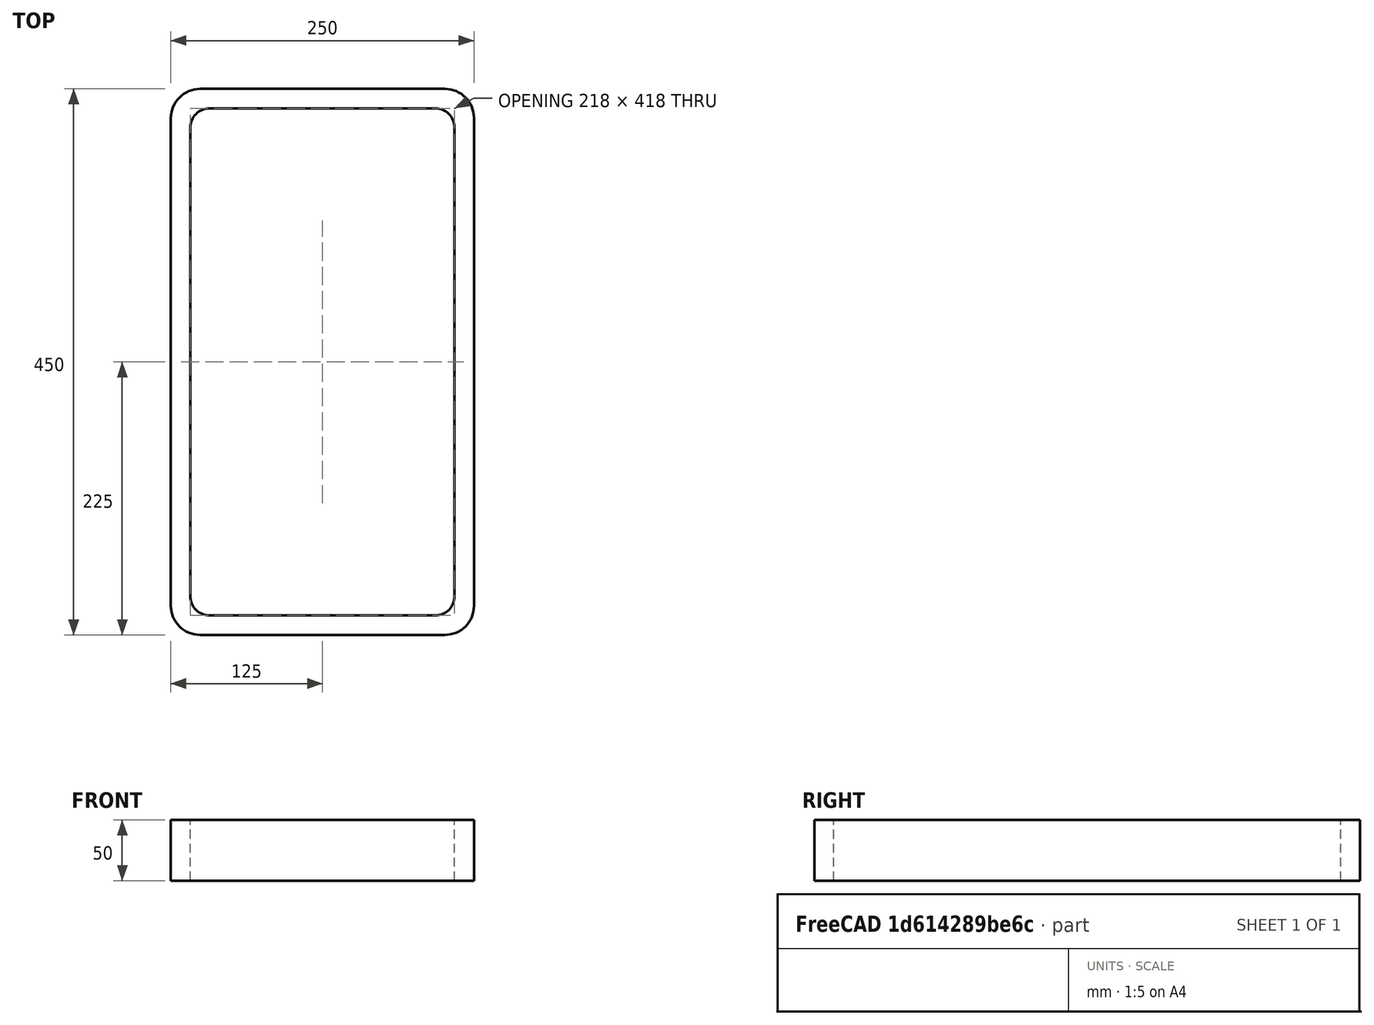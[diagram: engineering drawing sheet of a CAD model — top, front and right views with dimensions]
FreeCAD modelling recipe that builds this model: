
FCSTD DOCUMENT  (FreeCAD 0.15R4671 (Git))
Label: Rectangular hollow section 450x250x16 EN10219 S235JRH
License: All rights reserved
LicenseURL: http://en.wikipedia.org/wiki/All_rights_reserved
objects: Sketcher::SketchObject×1, Part::Extrusion×1
note: 2 computed .brp shape members not serialized (recipe doc carries the construction recipe); baked Part::Feature solids carry a one-line shape summary decoded from their .brp

FEATURE [Sketcher::SketchObject] Sketch
  sketch-geometry (16):
    g0: LineSegment StartX=-93 StartY=209 StartZ=0 EndX=93 EndY=209 EndZ=0
    g1: LineSegment StartX=109 StartY=193 StartZ=0 EndX=109 EndY=-193 EndZ=0
    g2: LineSegment StartX=93 StartY=-209 StartZ=0 EndX=-93 EndY=-209 EndZ=0
    g3: LineSegment StartX=-109 StartY=-193 StartZ=0 EndX=-109 EndY=193 EndZ=0
    g4: LineSegment StartX=-101 StartY=225 StartZ=0 EndX=101 EndY=225 EndZ=0
    g5: LineSegment StartX=125 StartY=201 StartZ=0 EndX=125 EndY=-201 EndZ=0
    g6: LineSegment StartX=101 StartY=-225 StartZ=0 EndX=-101 EndY=-225 EndZ=0
    g7: LineSegment StartX=-125 StartY=-201 StartZ=0 EndX=-125 EndY=201 EndZ=0
    g8: ArcOfCircle CenterX=-93 CenterY=193 CenterZ=0 NormalX=0 NormalY=0 NormalZ=1 Radius=16 StartAngle=1.5708 EndAngle=3.14159
    g9: ArcOfCircle CenterX=93 CenterY=193 CenterZ=0 NormalX=0 NormalY=0 NormalZ=1 Radius=16 StartAngle=0 EndAngle=1.5708
    g10: ArcOfCircle CenterX=93 CenterY=-193 CenterZ=0 NormalX=0 NormalY=0 NormalZ=1 Radius=16 StartAngle=4.71239 EndAngle=6.28319
    g11: ArcOfCircle CenterX=-93 CenterY=-193 CenterZ=0 NormalX=0 NormalY=0 NormalZ=1 Radius=16 StartAngle=3.14159 EndAngle=4.71239
    g12: ArcOfCircle CenterX=101 CenterY=201 CenterZ=0 NormalX=0 NormalY=0 NormalZ=1 Radius=24 StartAngle=0 EndAngle=1.5708
    g13: ArcOfCircle CenterX=101 CenterY=-201 CenterZ=0 NormalX=0 NormalY=0 NormalZ=1 Radius=24 StartAngle=4.71239 EndAngle=6.28319
    g14: ArcOfCircle CenterX=-101 CenterY=-201 CenterZ=0 NormalX=0 NormalY=0 NormalZ=1 Radius=24 StartAngle=3.14159 EndAngle=4.71239
    g15: ArcOfCircle CenterX=-101 CenterY=201 CenterZ=0 NormalX=0 NormalY=0 NormalZ=1 Radius=24 StartAngle=1.5708 EndAngle=3.14159
  constraints (36):
    c: Horizontal(g2)
    c: Vertical(g3)
    c: Horizontal(g6)
    c: Vertical(g7)
    c: Tangent(g3,g8) = 1.5708
    c: Tangent(g0,g8) = 1.5708
    c: Tangent(g0,g9) = 1.5708
    c: Tangent(g1,g9) = 1.5708
    c: Tangent(g1,g10) = 1.5708
    c: Tangent(g2,g10) = 1.5708
    c: Tangent(g2,g11) = 1.5708
    c: Tangent(g3,g11) = 1.5708
    c: Tangent(g4,g12) = 1.5708
    c: Tangent(g5,g12) = 1.5708
    c: Tangent(g5,g13) = 1.5708
    c: Tangent(g6,g13) = 1.5708
    c: Tangent(g6,g14) = 1.5708
    c: Tangent(g7,g14) = 1.5708
    c: Tangent(g7,g15) = 1.5708
    c: Tangent(g4,g15) = 1.5708
    c: Equal(g9,g8)
    c: Equal(g9,g11)
    c: Equal(g9,g10)
    c: Equal(g12,g15)
    c: Equal(g12,g14)
    c: Equal(g12,g13)
    c: Symmetric(g4,g6,g-1)
    c: Symmetric(g7,g5,g-2)
    c: DistanceY(g4,g6) = -450
    c: DistanceX(g7,g5) = 250
    c: Symmetric(g3,g1,g-2)
    c: Symmetric(g0,g2,g-1)
    c: DistanceY(g0,g4) = 16
    c: DistanceX(g5,g1) = -16
    c: Radius(g9) = 16
    c: Radius(g12) = 24
FEATURE [Part::Extrusion] Extrude  label="Rectangular hollow section 450x250x16 EN10219 S235JRH"
  Base = -> Sketch
  Dir = (0,0,50)
  Solid = true
